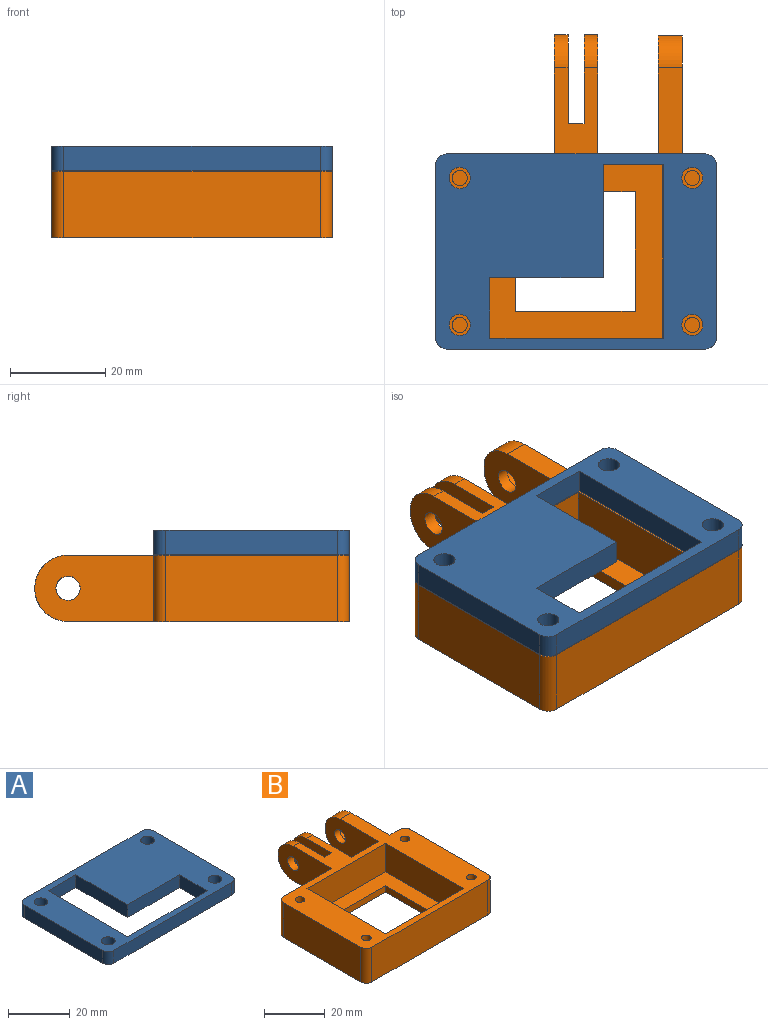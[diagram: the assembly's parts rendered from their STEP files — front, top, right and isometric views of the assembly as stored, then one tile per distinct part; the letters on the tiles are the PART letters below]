
ASSEMBLY  parts=2 mates=1
PART A: 20 faces, bbox 59x41x5.1 mm
  f0: plane 59x41.02mm, normal (0,0,1), area 1588.3mm2, adj f2,f3,f4,f5,f6,f7,f8,f9
  f1: plane 59x41.02mm, normal (0,0,-1), area 1588.3mm2, adj f2,f3,f4,f5,f6,f7,f8,f9
  f2: plane 35.94x5.08mm, normal (-1,0,0), area 182.6mm2, adj f0,f1,f6,f9
  f3: plane 53.92x5.08mm, normal (0,-1,0), area 273.9mm2, adj f0,f1,f6,f7
  f4: plane 35.94x5.08mm, normal (1,0,0), area 182.6mm2, adj f0,f1,f7,f8
  f5: plane 53.92x5.08mm, normal (0,1,0), area 273.9mm2, adj f0,f1,f8,f9
  f6: cylinder r=2.54mm len=5.08mm, axis (0,0,-1), area 20.3mm2, adj f0,f1,f2,f3
  f7: cylinder r=2.54mm len=5.08mm, axis (0,0,1), area 20.3mm2, adj f0,f1,f3,f4
  f8: cylinder r=2.54mm len=5.08mm, axis (0,0,-1), area 20.3mm2, adj f0,f1,f4,f5
  f9: cylinder r=2.54mm len=5.08mm, axis (0,0,1), area 20.3mm2, adj f0,f1,f2,f5
  f10: cylinder r=2.22mm len=5.08mm, axis (0,0,1), area 70.9mm2, adj f0,f1
  f11: cylinder r=2.22mm len=5.08mm, axis (0,0,1), area 70.9mm2, adj f0,f1
  f12: cylinder r=2.22mm len=5.08mm, axis (0,0,1), area 70.9mm2, adj f0,f1
  f13: cylinder r=2.22mm len=5.08mm, axis (0,0,1), area 70.9mm2, adj f0,f1
  f14: plane 36.45x5.08mm, normal (1,0,0), area 185.2mm2, adj f0,f1,f15,f19
  f15: plane 36.45x5.08mm, normal (0,1,0), area 185.2mm2, adj f0,f1,f14,f16
  f16: plane 12.7x5.08mm, normal (-1,0,0), area 64.5mm2, adj f0,f1,f15,f17
  f17: plane 23.75x5.08mm, normal (0,-1,0), area 120.6mm2, adj f0,f1,f16,f18
  f18: plane 23.75x5.08mm, normal (-1,0,0), area 120.6mm2, adj f0,f1,f17,f19
  f19: plane 12.7x5.08mm, normal (0,-1,0), area 64.5mm2, adj f0,f1,f14,f18
PART B: 49 faces, bbox 59x66x14 mm
  f0: plane 24.77x13.97mm, normal (1,0,0), area 239.3mm2, adj f2,f3,f4,f5,f42,f43,f44,f45
  f1: cylinder r=2.54mm len=5.08mm, axis (-1,0,0), area 40.5mm2, adj f41,f48
  f2: plane 5.08x3.73mm, normal (0,1,0), area 19mm2, adj f0,f41,f42,f43
  f3: plane 59.06x59mm, normal (0,0,1), area 1272mm2, adj f0,f5,f6,f7,f8,f9,f10,f11
  f4: plane 59.06x59mm, normal (0,0,-1), area 1999.9mm2, adj f0,f5,f6,f7,f8,f9,f10,f11
  f5: plane 13.97x4.6mm, normal (0,1,0), area 64.2mm2, adj f0,f3,f4,f14
  f6: cylinder r=6.99mm len=13.97mm, axis (1,0,0), area 63.5mm2, adj f3,f4,f33,f38
  f7: plane 13.97x12.7mm, normal (0,1,0), area 177.4mm2, adj f3,f4,f33,f41
  f8: plane 35.94x13.97mm, normal (-1,0,0), area 502.1mm2, adj f3,f4,f12,f15
  f9: plane 53.92x13.97mm, normal (0,-1,0), area 753.3mm2, adj f3,f4,f12,f13
  f10: plane 35.94x13.97mm, normal (1,0,0), area 502.1mm2, adj f3,f4,f13,f14
  f11: plane 22.4x13.97mm, normal (0,1,0), area 313mm2, adj f3,f4,f15,f34
  f12: cylinder r=2.54mm len=13.97mm, axis (0,0,-1), area 55.7mm2, adj f3,f4,f8,f9
  f13: cylinder r=2.54mm len=13.97mm, axis (0,0,1), area 55.7mm2, adj f3,f4,f9,f10
  f14: cylinder r=2.54mm len=13.97mm, axis (0,0,-1), area 55.7mm2, adj f3,f4,f5,f10
  f15: cylinder r=2.54mm len=13.97mm, axis (0,0,1), area 55.7mm2, adj f3,f4,f8,f11
  f16: plane 36.45x11.43mm, normal (1,0,0), area 416.6mm2, adj f3,f17,f19,f20
  f17: plane 36.45x11.43mm, normal (0,1,0), area 416.6mm2, adj f3,f16,f18,f20
  f18: plane 36.45x11.43mm, normal (-1,0,0), area 416.6mm2, adj f3,f17,f19,f20
  f19: plane 36.45x11.43mm, normal (0,-1,0), area 416.6mm2, adj f3,f16,f18,f20
  f20: plane 36.45x36.45mm, normal (0,0,1), area 696.2mm2, adj f16,f17,f18,f19,f21,f22,f23,f24
  f21: plane 25.15x2.54mm, normal (1,0,0), area 63.9mm2, adj f4,f20,f22,f24
  f22: plane 25.15x2.54mm, normal (0,1,0), area 63.9mm2, adj f4,f20,f21,f23
  f23: plane 25.15x2.54mm, normal (-1,0,0), area 63.9mm2, adj f4,f20,f22,f24
  f24: plane 25.15x2.54mm, normal (0,-1,0), area 63.9mm2, adj f4,f20,f21,f23
  f25: cylinder r=1.59mm len=12.7mm, axis (0,0,1), area 126.7mm2, adj f3,f26
  f26: plane 3.18x3.18mm, normal (0,0,1), area 7.9mm2, adj f25
  f27: cylinder r=1.59mm len=12.7mm, axis (0,0,1), area 126.7mm2, adj f3,f28
  f28: plane 3.18x3.18mm, normal (0,0,1), area 7.9mm2, adj f27
  f29: cylinder r=1.59mm len=12.7mm, axis (0,0,1), area 126.7mm2, adj f3,f30
  f30: plane 3.18x3.18mm, normal (0,0,1), area 7.9mm2, adj f29
  f31: cylinder r=1.59mm len=12.7mm, axis (0,0,1), area 126.7mm2, adj f3,f32
  f32: plane 3.18x3.18mm, normal (0,0,1), area 7.9mm2, adj f31
  f33: plane 25.02x13.97mm, normal (1,0,0), area 308.3mm2, adj f3,f4,f6,f7,f39
  f34: plane 25.02x13.97mm, normal (-1,0,0), area 308.3mm2, adj f3,f4,f11,f35,f40
  f35: cylinder r=6.99mm len=13.97mm, axis (1,0,0), area 63.5mm2, adj f3,f4,f34,f37
  f36: plane 13.97x3.35mm, normal (0,1,0), area 46.8mm2, adj f3,f4,f37,f38
  f37: plane 18.67x13.97mm, normal (1,0,0), area 219.6mm2, adj f3,f4,f35,f36,f40
  f38: plane 18.67x13.97mm, normal (-1,0,0), area 219.6mm2, adj f3,f4,f6,f36,f39
  f39: cylinder r=2.54mm len=5.08mm, axis (1,0,0), area 46.2mm2, adj f33,f38
  f40: cylinder r=2.54mm len=5.08mm, axis (1,0,0), area 46.2mm2, adj f34,f37
  f41: plane 24.77x13.97mm, normal (-1,0,0), area 307.7mm2, adj f1,f2,f3,f4,f7,f42,f43
  f42: cylinder r=6.99mm len=6.73mm, axis (-1,0,0), area 46.1mm2, adj f0,f2,f4,f41
  f43: cylinder r=6.99mm len=6.73mm, axis (-1,0,0), area 46.1mm2, adj f0,f2,f3,f41
  f44: plane 11.26x2.54mm, normal (0,0.14,-0.99), area 28.9mm2, adj f0,f45,f47,f48
  f45: cylinder r=1.91mm len=3.81mm, axis (1,0,0), area 15.2mm2, adj f0,f44,f46,f48
  f46: plane 11.27x2.54mm, normal (0,0.14,0.99), area 28.9mm2, adj f0,f45,f47,f48
  f47: cylinder r=3.49mm len=6.99mm, axis (1,0,0), area 30.3mm2, adj f0,f44,f46,f48
  f48: plane 17.15x6.99mm, normal (1,0,0), area 68.4mm2, adj f1,f44,f45,f46,f47
PLACE A rot(axis=(0,1,0),180deg) t=(-2.94,-12.46,6.5)mm
PLACE B t=(-11.14,-12.46,-12.66)mm
MATE cylindrical A.f12 <-> B.f31  axis (0,0,-1) through (-31.46,-23,6.5)mm
